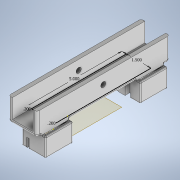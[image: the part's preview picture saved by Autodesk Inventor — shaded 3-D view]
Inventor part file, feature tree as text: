
AUTODESK INVENTOR PART (.ipt)
format: ipt  version: 2020 (Build 240168000, 168)  size: 911,872 bytes
history: native  units: in
note: dims shown in document units (in); Inventor stores cm internally (conversion verified against a paired STEP export)
features: sketch x11, extrude x9, hole x3, fillet x3, projected_geometry x2, plane x1, split x1
ambient origin geometry x8: Origin, YZ Plane, XZ Plane, XY Plane, X Axis, Y Axis, Z Axis, Center Point
bodies: Solid1 (feature_tree)
feature tree (30):
  sketch  "Sketch1"  dims[d0=1.5in d1=5.0in]
  extrude  "Extrusion1"  Depth=5.0in
  extrude  "Extrusion2"  Depth=0.2in
  hole  "Hole1"  [1 undecoded]
  extrude  "Extrusion3"  Depth=0.75in
  hole  "Hole2"  [1 undecoded]
  fillet  "Fillet1"  Radius=0.125in
  extrude  "Extrusion4"  Depth=0.125in TaperAngle=0.0deg
  extrude  "Extrusion5"  Depth=0.125in
  sketch  "Sketch10"  dims[d17=1.0in d18=0.75in d19=0.125in]
  plane  "Work Plane2"
  split  "Split1"
  hole  "Hole5"  [1 undecoded]
  extrude  "Extrusion6"  Depth=0.0625in
  extrude  "Extrusion7"  TaperAngle=90.0deg  [1 undecoded]
  extrude  "Extrusion8"  Depth=0.0625in
  extrude  "Extrusion9"  Depth=0.0625in
  fillet  "Fillet2"  Radius=0.125in
  fillet  "Fillet3"  Radius=0.075in
  sketch  "Sketch2"  dims[d2=0.2in d3=0.2in]
  sketch  "Sketch3"  dims[d4=1.0in d5=0.0in d6=0.2in d7=0.0in]
  sketch  "Sketch5"  dims[d8=0.5in]
  sketch  "Sketch6"  dims[d9=0.266in d10=0.75in d11=0.438in d12=0.25in d13=0.5635in d14=1.0in d15=0.8108in d16=0.75in]
  sketch  "Sketch11"  dims[d20=0.125in d21=1.0in d22=0.0in]
  sketch  "Sketch12"  dims[d23=0.25in]
  projected_geometry  "Projected Loop1"
  sketch  "Sketch13"  dims[d24=0.0591in d25=0.75in d26=0.438in d27=0.25in d28=0.5635in d29=1.0in d30=0.8108in d31=0.125in]
  projected_geometry  "Projected Loop2"
  sketch  "Sketch14"  dims[d32=0.125in d33=0.125in]
  sketch  "Sketch15"  dims[d34=0.75in d35=0.75in d36=90.0deg d37=0.1in d38=0.1in d39=0.125in d40=0.075in d41=0.25in d42=3.25in d43=0.0in d44=0.05in d45=0.0in d46=0.5in d47=0.5in d48=0.75in d49=0.375in d50=0.375in d51=0.375in d67=0.188in d68=0.188in d69=0.188in d70=0.089in d71=0.75in d72=0.375in d73=0.25in d74=0.5635in d75=0.25in d76=0.8108in d77=0.188in d78=0.188in d79=0.188in d80=0.188in d81=1.0in d82=0.0in d83=1.0in d84=0.0in d85=1.2in d86=0.2in d87=0.8in d88=0.188in d89=0.188in d90=0.125in d91=0.125in d92=0.125in d93=0.6in d94=0.125in d95=1.0in d96=0.0in d97=0.0625in d98=180.0deg d99=0.125in d100=0.5in d101=0.0in d102=0.2in d103=1.2in d104=0.8in d105=1.2in d106=0.125in d107=0.475in d108=0.125in d109=0.125in d110=0.125in d111=0.125in d112=0.0625in]
note: 4 required parameter values undecoded (feature->parameter linkage not recoverable at this tier; creation-order binding heuristic only, values carry confidence <= 0.55)
